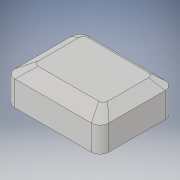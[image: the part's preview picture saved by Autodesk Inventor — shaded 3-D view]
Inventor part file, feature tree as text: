
AUTODESK INVENTOR PART (.ipt)
format: ipt  version: 2017 (Build 210142000, 142)  size: 673,280 bytes
history: native  units: in
note: dims shown in document units (in); Inventor stores cm internally (conversion verified against a paired STEP export)
features: sketch x24, extrude x18, other x8, fillet x5, loft x3, mirror x1, plane x1
ambient origin geometry x8: Origin, YZ Plane, XZ Plane, XY Plane, X Axis, Y Axis, Z Axis, Center Point
bodies: Solid1 (feature_tree)
feature tree (60):
  extrude  "middle of body"  Depth=1.276in
  other  "top of printer"
  loft  "top part of printer"
  extrude  "keys for printer"  Depth=0.1257in
  other  "Bottom of printer"
  loft  "bottom part of printer"
  extrude  "front bottom door slot"  Depth=0.151in
  extrude  "front top door slot"  TaperAngle=0.0deg  [1 undecoded]
  extrude  "cords cut"  Depth=0.7135in
  extrude  "cords join curve part"  Depth=0.1007in
  extrude  "paper eject slot"  TaperAngle=0.0deg  [1 undecoded]
  other  "paper eject curve up and out"
  extrude  "2nd to top slot"  Depth=0.3692in
  extrude  "2nd to bottom slot"  Depth=0.0833in
  extrude  "top slot"  Depth=0.06in
  extrude  "slot for paper rezevor"  Depth=0.0157in
  extrude  "seams for paper rezevor"  Depth=0.0481in
  other  "door axle"
  mirror  "axle for door"
  sketch  "Sketch26"  dims[d39=0.1506in d40=0.0481in]
  other  "end of door connection"
  loft  "connection from door axle to door"
  plane  "Work Plane8"
  extrude  "tray"  Depth=0.0682in
  extrude  "curve to tray to match receive"  Depth=0.0437in
  extrude  "curve to tray to match receive top"  Depth=0.0725in
  extrude  "extention for paper slot"  Depth=0.1404in TaperAngle=0.0deg
  other  "bottom of extention for paper"
  extrude  "extention for paper"  Depth=0.1207in
  extrude  "extention for paper retract area"  Depth=0.474in
  fillet  "curve 2nd from bottom"  [1 undecoded]
  fillet  "curve top and 2nd from top"  Radius=0.3776in
  fillet  "curve extention for door"  Radius=0.0892in
  fillet  "curve door, receive door, and axles"  Radius=0.2029in
  fillet  "smooth slots"  [1 undecoded]
  sketch  "Sketch1"  dims[d3=0.151in d4=1.276in]
  sketch  "Sketch2"  dims[d5=0.151in d6=0.8125in]
  other  "Edges1"
  sketch  "Sketch3"  dims[d7=0.4346in d8=0.0in d9=0.1257in]
  other  "Edges2"
  sketch  "Sketch4"  dims[d10=0.6016in d11=0.8594in]
  sketch  "Sketch5"  dims[d12=0.151in d13=0.0755in]
  sketch  "Sketch7"  dims[d14=0.0in d15=90.0deg d16=0.0in d17=90.0deg]
  sketch  "Sketch9"  dims[d18=0.1785in d19=0.7135in]
  sketch  "Sketch15"  dims[d21=0.0833in d22=0.1007in]
  sketch  "Sketch21"  dims[d23=0.0in d24=90.0deg d25=0.0in d26=90.0deg]
  sketch  "Sketch22"  dims[d27=0.3846in d30=0.3692in]
  sketch  "Sketch23"  dims[d31=0.1158in d32=0.0in d33=0.0833in]
  sketch  "Sketch24"  dims[d34=0.1158in d35=0.0in d36=0.06in]
  sketch  "Sketch25"  dims[d37=0.0215in d38=0.0157in]
  sketch  "Sketch28"  dims[d43=0.0618in d46=0.0175in]
  sketch  "Sketch29"  dims[d47=0.0361in d48=0.0682in]
  sketch  "Sketch30"  dims[d49=0.2541in d50=0.0in d57=0.0437in]
  sketch  "Sketch31"  dims[d62=0.0142in d63=0.0725in]
  sketch  "Sketch32"  dims[d64=0.0505in d65=0.1404in d66=0.0in]
  sketch  "Sketch33"  dims[d87=1.3229in d96=0.1207in]
  sketch  "Sketch34"  dims[d97=0.0985in d98=0.474in d99=90.0deg d116=0.3776in d117=0.0892in d118=0.2029in d119=0.0in d120=180.0deg]
  sketch  "Sketch35"  dims[d121=0.3013in]
  sketch  "Sketch37"  dims[d122=0.0706in]
  sketch  "Sketch39"  dims[d123=0.0645in d124=0.0in d125=0.0327in d126=0.0758in d127=0.0143in d128=0.0in d129=0.1667in d130=0.0308in d131=0.0in d138=0.0618in d139=0.0061in d140=0.0in d141=90.0deg d142=0.0in d143=90.0deg d144=0.0344in d146=0.0618in d147=0.0in d153=0.089in d154=0.2541in d155=0.5725in d164=0.017in d165=0.0361in d167=0.0618in d168=0.0in d174=0.0142in d175=0.0725in d176=0.051in d177=0.1404in d178=0.0in d179=0.4179in d180=0.0282in d181=0.1717in d182=0.0134in d183=0.1865in d184=0.0in d185=-0.1775in d186=0.1775in d187=0.024in d188=0.0021in d189=0.5209in d190=0.0in d191=0.1796in d192=0.1796in d193=0.0in d194=0.0133in d195=0.0251in d197=0.0251in d198=0.003in d199=0.003in d201=0.0612in d202=0.0612in d203=0.012in d204=0.3333in d206=0.094in d207=0.0in d218=0.006in d219=0.006in d220=0.006in d221=0.001in d222=0.0in d223=0.3254in d224=0.2719in d226=0.0022in d227=0.0022in d229=0.0022in d230=0.0022in d232=0.0022in d236=0.0022in d238=0.0022in d243=0.0022in d244=0.0022in d245=0.0022in d246=0.0022in d247=0.0022in d248=0.0022in d249=1.1811in d251=360.0deg d253=0.0022in d270=0.0022in d271=0.0022in d272=0.005in d273=0.0in d274=0.0318in d275=0.0073in d276=0.0022in d278=0.0011in d279=0.0022in d280=0.0022in d281=0.0022in d282=0.0022in d283=0.0022in d284=0.1306in d285=0.1306in d286=0.0022in d287=0.0022in d288=0.2002in d289=0.1512in d290=0.0022in d291=0.0022in d292=0.0022in d293=0.0022in d294=0.0022in d295=0.0022in d297=0.0194in d298=0.0035in d299=0.0022in d300=0.0135in d301=0.0503in d302=0.0808in d305=0.0774in d306=0.0352in d308=0.0968in d309=0.0109in d310=0.0022in d311=0.0043in d312=0.0043in d313=0.0022in d314=0.0022in d315=0.0022in d316=0.0022in d317=0.0667in d318=0.0667in d319=0.0135in d320=0.0785in d321=0.0203in d322=0.0203in d323=0.0022in d324=0.0296in d325=0.0619in d327=0.0299in d328=0.0295in d329=0.032in d331=0.0415in d332=0.0336in d333=0.0163in]
note: 4 required parameter values undecoded (feature->parameter linkage not recoverable at this tier; creation-order binding heuristic only, values carry confidence <= 0.55)
